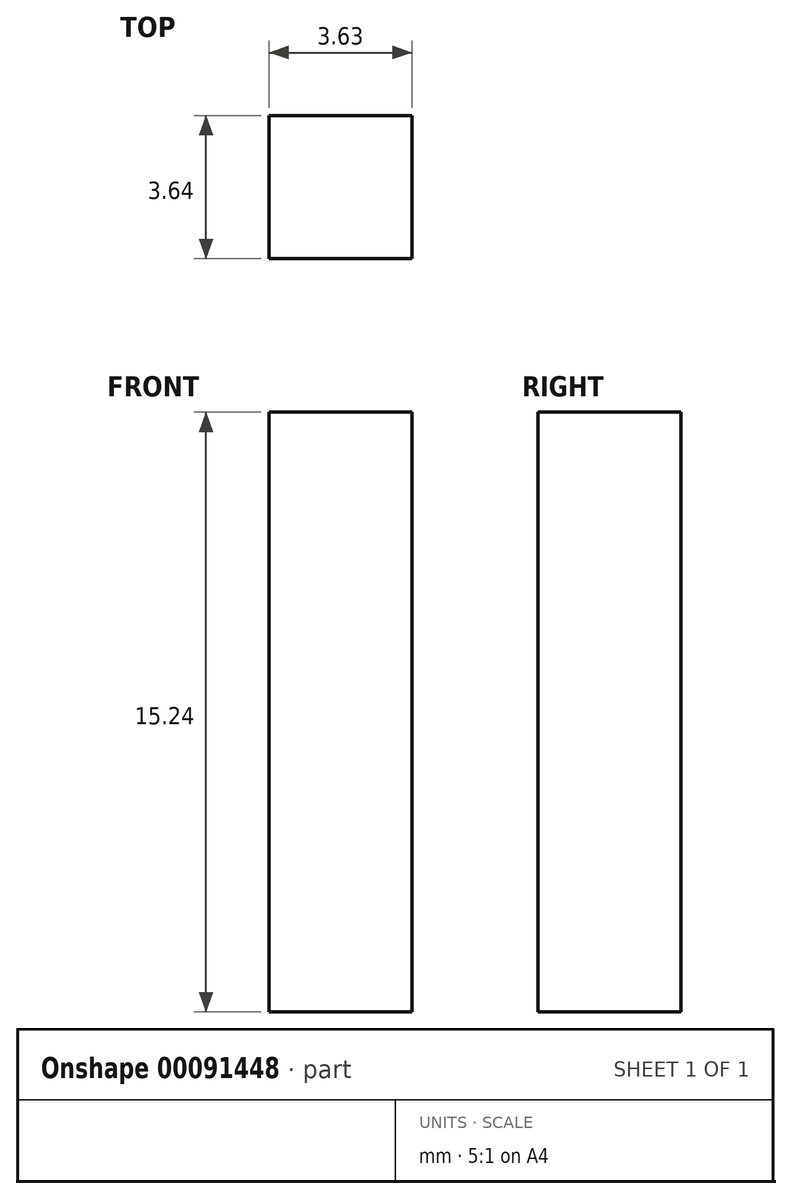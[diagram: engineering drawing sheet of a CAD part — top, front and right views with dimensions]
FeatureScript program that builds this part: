
annotation { "Feature Type Name" : "Feature", "Feature Type Description" : "" }
export const myFeature = defineFeature(function(context is Context, id is Id, definition is map)
    precondition{}
    {
        {
            var Q0;
            Q0=qCreatedBy(makeId("Top.planeOp"),FACE);
            var sketch = newSketch(context, id + "F0", { "sketchPlane" : qUnion([Q0])});
            skLineSegment(sketch, "E0.bottom", {"start": v(-17.33, 0.35) * mm, "end": v(-13.7, 0.35) * mm});
            skLineSegment(sketch, "E0.top", {"start": v(-17.33, -3.29) * mm, "end": v(-13.7, -3.29) * mm});
            skLineSegment(sketch, "E0.left", {"start": v(-17.33, 0.35) * mm, "end": v(-17.33, -3.29) * mm});
            skLineSegment(sketch, "E0.right", {"start": v(-13.7, 0.35) * mm, "end": v(-13.7, -3.29) * mm});
            skPoint(sketch, "E1", {"position": v(-17.33, -3.29) * mm});
            skPoint(sketch, "E2", {"position": v(-13.7, -3.29) * mm});
            skSolve(sketch);
        }
        {
            var Q0;
            Q0=makeQuery(id+"F0.imprint","IMPRINT",FACE,{"disambiguationData":[TD([[makeQuery(id+"F0.imprint","IMPRINT",EDGE,{"derivedFrom":sQuery(id+"F0.wireOp",EDGE,"E0.bottom")}),-1.0]])]});
            extrude(context, id + "F1", {"entities" : qUnion([Q0]), "depth" : 15.24 * mm});
        }
    });
